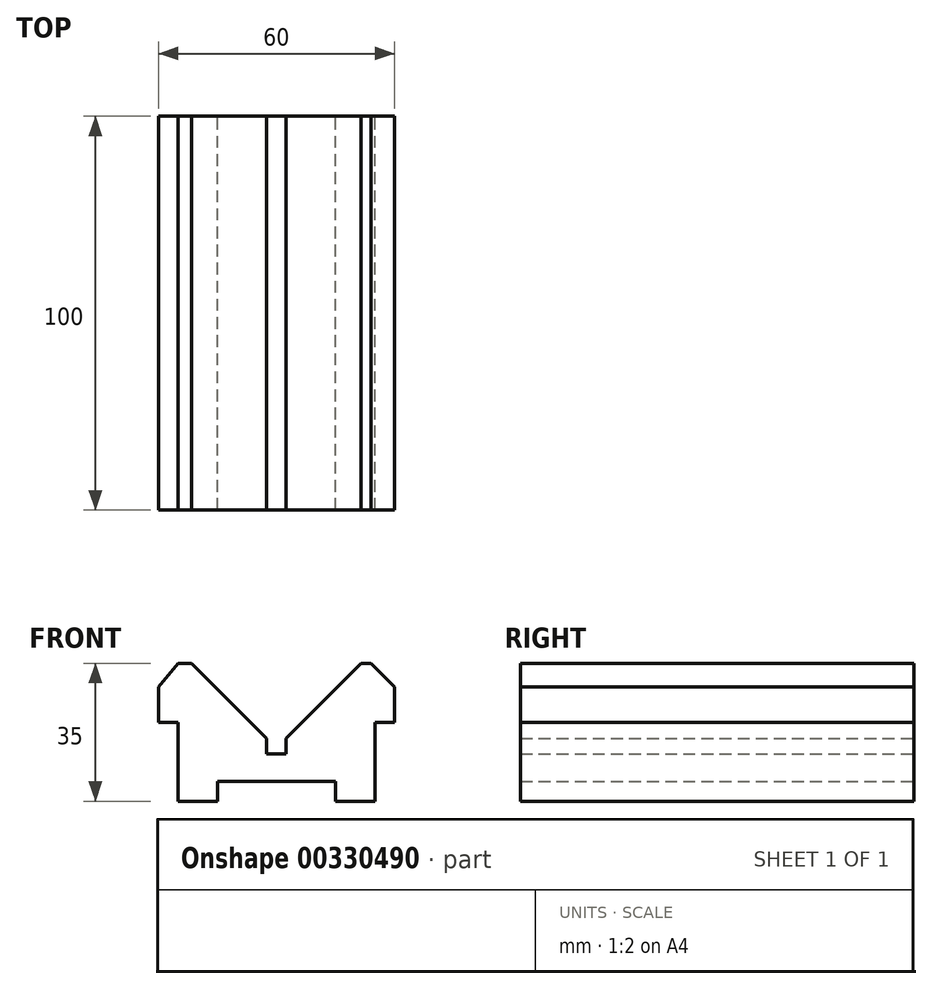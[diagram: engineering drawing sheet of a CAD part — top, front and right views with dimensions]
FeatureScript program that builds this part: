
annotation { "Feature Type Name" : "Feature", "Feature Type Description" : "" }
export const myFeature = defineFeature(function(context is Context, id is Id, definition is map)
    precondition{}
    {
        {
            var Q0;
            Q0=qCreatedBy(makeId("Front.planeOp"),FACE);
            var sketch = newSketch(context, id + "F0", { "sketchPlane" : qUnion([Q0])});
            skLineSegment(sketch, "E0", {"start": v(-15, 0) * mm, "end": v(15, 0) * mm});
            skLineSegment(sketch, "E1", {"start": v(15, 0) * mm, "end": v(15, -5) * mm});
            skLineSegment(sketch, "E2", {"start": v(15, -5) * mm, "end": v(25, -5) * mm});
            skLineSegment(sketch, "E3", {"start": v(25, -5) * mm, "end": v(25, 15) * mm});
            skLineSegment(sketch, "E4", {"start": v(25, 15) * mm, "end": v(30, 15) * mm});
            skLineSegment(sketch, "E5", {"start": v(30, 15) * mm, "end": v(30, 24) * mm});
            skLineSegment(sketch, "E6", {"start": v(30, 24) * mm, "end": v(24, 30) * mm});
            skLineSegment(sketch, "E7", {"start": v(24, 30) * mm, "end": v(21.5, 30) * mm});
            skLineSegment(sketch, "E8", {"start": v(21.5, 30) * mm, "end": v(2.5, 11) * mm});
            skLineSegment(sketch, "E9", {"start": v(2.5, 11) * mm, "end": v(2.5, 7) * mm});
            skLineSegment(sketch, "E10", {"start": v(2.5, 7) * mm, "end": v(-2.5, 7) * mm});
            skLineSegment(sketch, "E11", {"start": v(-2.5, 7) * mm, "end": v(-2.5, 11) * mm});
            skLineSegment(sketch, "E12", {"start": v(-2.5, 11) * mm, "end": v(-21.5, 30) * mm});
            skLineSegment(sketch, "E13", {"start": v(-21.5, 30) * mm, "end": v(-25, 30) * mm});
            skLineSegment(sketch, "E14", {"start": v(-30, 24) * mm, "end": v(-25, 30) * mm});
            skLineSegment(sketch, "E15", {"start": v(-30, 24) * mm, "end": v(-30, 15) * mm});
            skLineSegment(sketch, "E16", {"start": v(-30, 15) * mm, "end": v(-25, 15) * mm});
            skLineSegment(sketch, "E17", {"start": v(-25, 15) * mm, "end": v(-25, -5) * mm});
            skLineSegment(sketch, "E18", {"start": v(-25, -5) * mm, "end": v(-15, -5) * mm});
            skLineSegment(sketch, "E19", {"start": v(-15, -5) * mm, "end": v(-15, 0) * mm});
            skPoint(sketch, "E20", {"position": v(0, 7) * mm});
            skSolve(sketch);
        }
        {
            var Q0;
            Q0=makeQuery(id+"F0.imprint","IMPRINT",FACE,{"disambiguationData":[TD([[makeQuery(id+"F0.imprint","IMPRINT",EDGE,{"derivedFrom":sQuery(id+"F0.wireOp",EDGE,"E0")}),1.0]])]});
            extrude(context, id + "F1", {"entities" : qUnion([Q0]), "depth" : 100 * mm});
        }
    });
